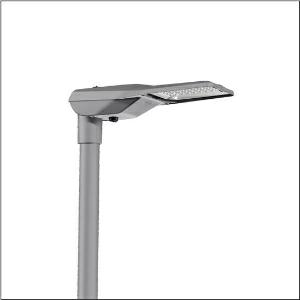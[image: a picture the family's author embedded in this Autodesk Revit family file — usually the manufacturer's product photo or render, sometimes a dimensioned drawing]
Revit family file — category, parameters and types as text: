
# Revit family: streetlight_sl_21_mini___st1_5a_5xe2p33t08hb_306c
name_source: partatom
category: Lighting Fixtures
units: mm (PartAtom-declared; Revit-internal decimal feet)

## family parameters
Cut with Voids When Loaded = No
Host = Face
Light Source = No
Part Type = Normal
Room Calculation Point = No
Round Connector Dimension = Use Diameter
Shared = No

## types (1)
- --- (1 x LED, 8890 lm, 66 W, 3000K)
    Apparent Load = 66 VA
    CIE Flux Codes = 22 53 95 100 100
    Color Rendering = 70
    Color Temperature = 3000K
    Default Elevation = 1800 mm
    Description = Streetlight SL 21 mini, mast luminaire, primary light control with lens, of PMMA, primary optical cover: cover, of toughened safety glass, transparent, light distribution: ST1.5a, light emission: direct distribution, primary light characteristic: asymmetric, installation type: side-entry, post-top, LED, High Power LED, rated luminous flux: 8.890lm, luminous efficacy: 135lm/W, light colour: 730, colour temperature: 3000K, control gear: D4i, control: overheat protection, constant luminous flux control, time-dependent luminous flux control, flexible luminous flux parameterisation, pre-setting: logarithmic dimming characteristic, mains connection: 220..240V, AC, 50/60Hz, start of lifetime: 66W, end of service life: 69W, reduction: 30W, luminaire housing, of diecast aluminium, powder-coated, Siteco® metallic grey (DB 702S), corrosivity category C5 high according to DIN EN ISO 12944, please order mast flange separately, inclination adjustable: 0°, 5°, 10°, 15°, sealing non-destructively replaceable, multi-level sealing system, length: 628mm, width: 235mm, height: 110mm, mast flange for spigot size: 42mm (side-entry): 5XC10008XM4, 60/48mm (side-entry/post-top): 5XC10108XM2, 76/60mm (side-entry/post-top): 5XC10108XM1, mounting height: 4..8m, Smart Interface below and above, protection rating (complete): IP66, insulation class (complete): insulation class II (safety insulation), certification: CE, ENEC, ENEC+, VDE, impact resistance: IK10, permissible operating ambient temperature for outdoor applications: -40..+50°C, standard-compliant lighting for roads and squares, packaging unit: 1 piece

Light Distribution: ST1.5a
    Height = 110 mm
    Lamp = 1 x LED
    Lamp Light Flux = 8890 lm
    Lamp Power = 66 W
    Lamp count = 1
    Length = 625 mm
    Luminous efficacy = 135 lm/W
    Manufacturer = Siteco
    ModVariant = No
    Model = 5XE2P33T08HB
    Number of Poles = 1
    OnlyDefault = Yes
    Power Factor = 1
    Product Name = Streetlight SL 21 mini | ST1.5a
    Product group = mast luminaire | pylon top
    ProductGroupID = 6100
    Protection Class = Protection class II
    Protection Degree = IP 66
    RLX_Detail_Level = 1
    RLX_Emergency_Light_Flux = 0 lm
    RLX_Emergency_Type = 0
    RLX_Emergency_Type_DB = No
    RlxData = <blob elided: 29777 chars, md5=450ca313>
    Socket = socket
    Standby Power = 0 W
    System Light Flux = 8890 lm
    System Power = 66 W
    Type Comments = factory setting: luminous flux: 100 % | dim-lin: 254 | 670 mA
    Type Image = l_1003514.jpg
    URL = http://relux.com
    VarID = @adj_178759
    Voltage = 0 V
    Weight = 0.00 kg
    Width = 234 mm

## geometry (parser evidence)
native form markers: Blend x4, Sweep x10
no freeform markers — native parametric forms only
